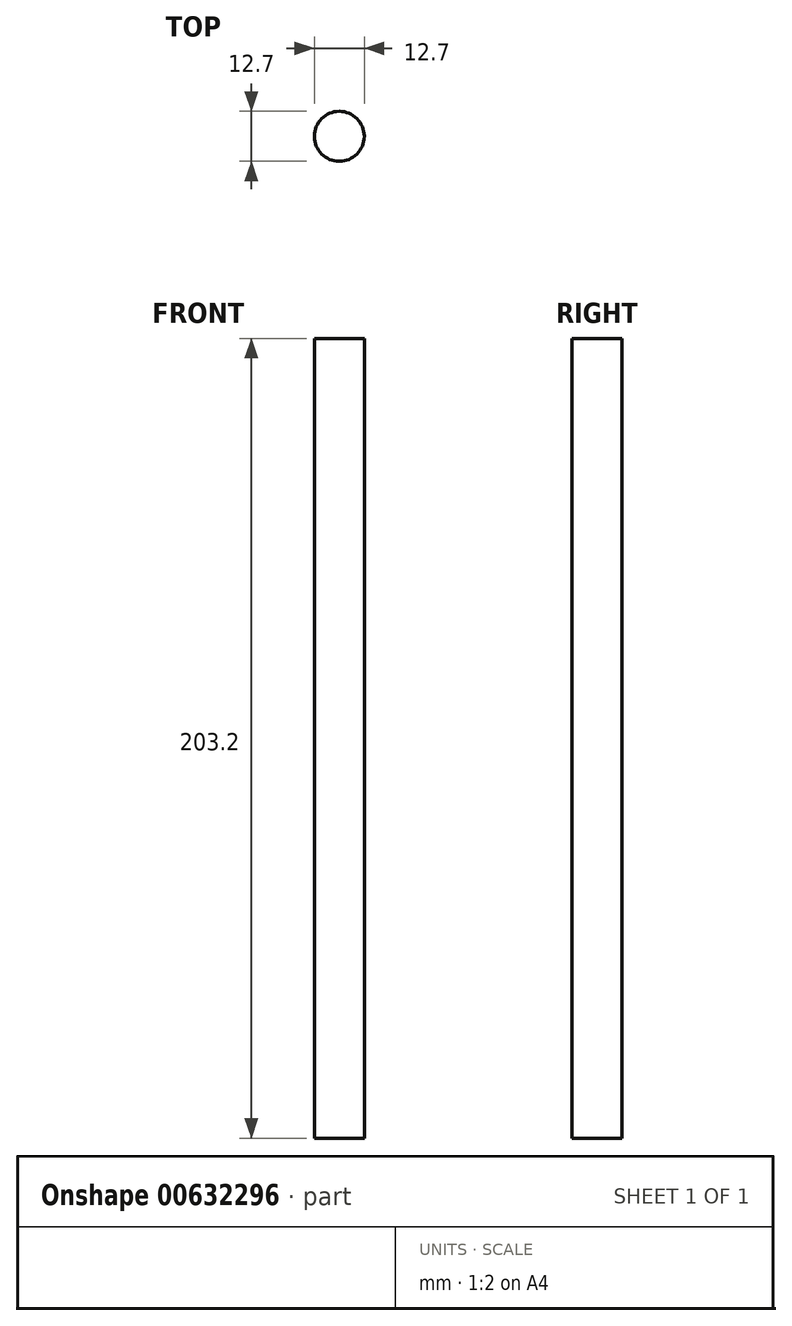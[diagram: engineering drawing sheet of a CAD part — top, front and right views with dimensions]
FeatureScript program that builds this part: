
annotation { "Feature Type Name" : "Feature", "Feature Type Description" : "" }
export const myFeature = defineFeature(function(context is Context, id is Id, definition is map)
    precondition{}
    {
        {
            var Q0;
            Q0=qCreatedBy(makeId("Top.planeOp"),FACE);
            var sketch = newSketch(context, id + "F0", { "sketchPlane" : qUnion([Q0])});
            skCircle(sketch, "E0", {"center": v(-39, 14.94) * mm, "radius": 6.35 * mm});
            skSolve(sketch);
        }
        {
            var Q0;
            Q0 = qSketchRegion(id + "F0", true);
            extrude(context, id + "F1", {"entities" : qUnion([Q0]), "endBound" : BoundingType.SYMMETRIC, "depth" : 203.2 * mm, "offsetDistance" : 25.4 * mm});
        }
    });
